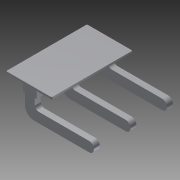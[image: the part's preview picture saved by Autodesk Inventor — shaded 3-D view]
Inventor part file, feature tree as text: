
AUTODESK INVENTOR PART (.ipt)
format: ipt  version: 2011 SP1 (Build 150282100, 282)  size: 131,072 bytes
history: native  units: in
note: dims shown in document units (in); Inventor stores cm internally (conversion verified against a paired STEP export)
features: other x7, extrude x2, sketch x2, pattern_linear x1
ambient origin geometry x8: Origin, YZ Plane, XZ Plane, XY Plane, X Axis, Y Axis, Z Axis, Center Point
bodies: Solid1 (feature_tree)
feature tree (12):
  extrude  "Extrusion1"  Depth=0.03in TaperAngle=0.0deg
  extrude  "Extrusion2"  [1 undecoded]
  pattern_linear  "Rectangular Pattern1"  [2 undecoded]
  other  "to_base_XY"
  other  "to_base_YZ"
  other  "to_base_ZX"
  other  "to_base_X"
  other  "to_base_Y"
  other  "to_base_Z"
  other  "to_base_Center"
  sketch  "Sketch_2"  dims[d4=1.1811in d6=0.185in d7=0.3937in d9=0.0in]
  sketch  "Sketch_1"  dims[d0=0.01in d1=0.0in d2=0.03in d3=0.0in]
note: 3 required parameter values undecoded (feature->parameter linkage not recoverable at this tier; creation-order binding heuristic only, values carry confidence <= 0.55)
